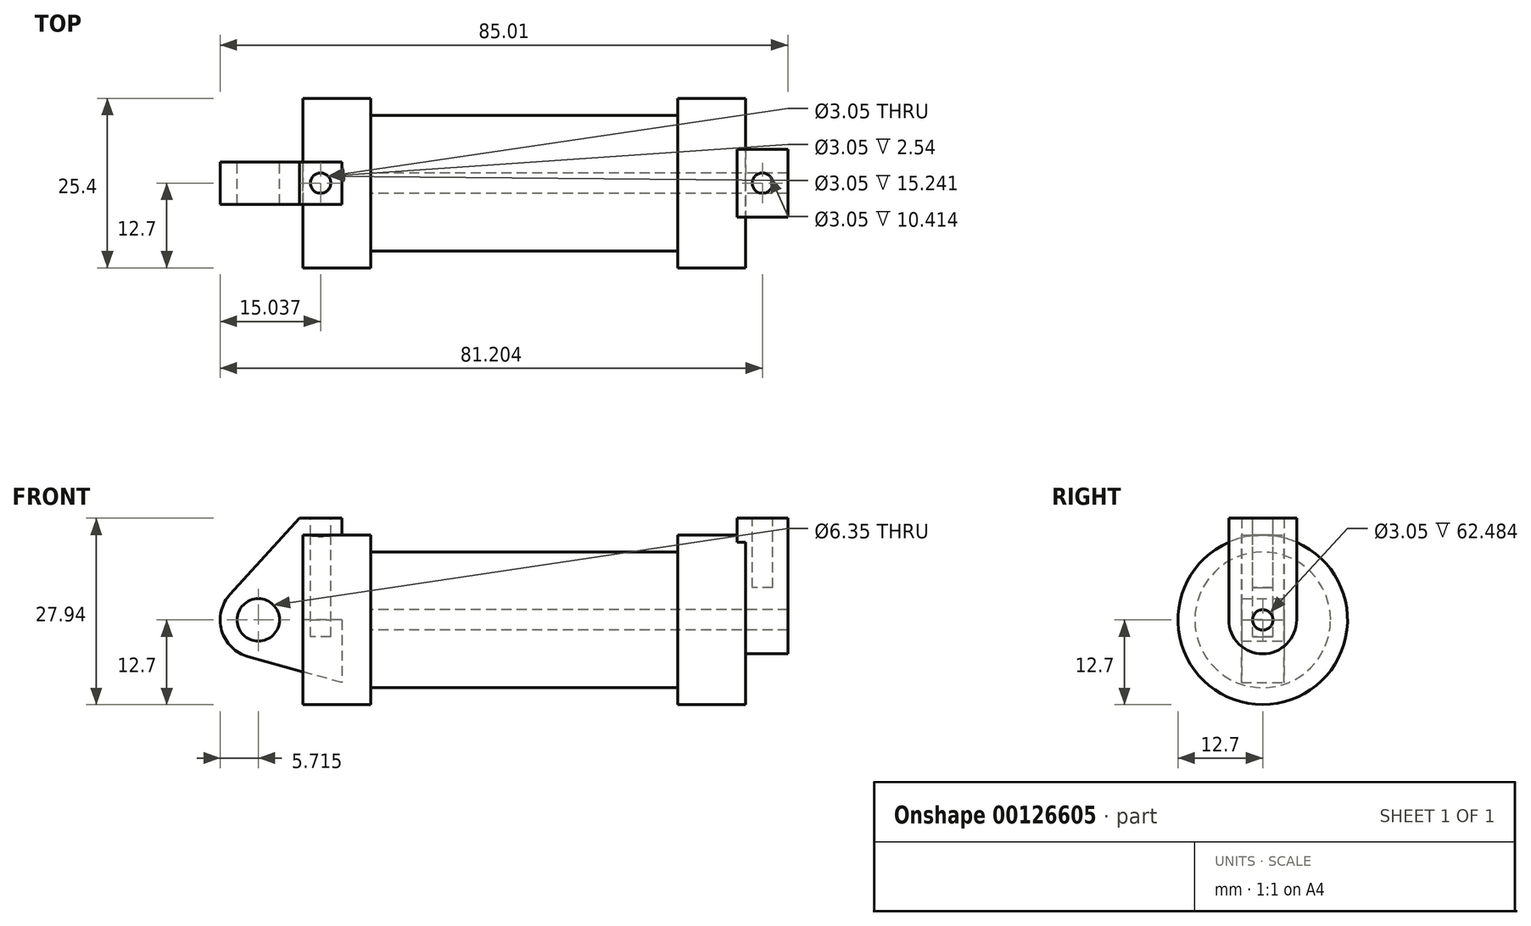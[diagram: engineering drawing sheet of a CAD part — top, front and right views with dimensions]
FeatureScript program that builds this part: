
annotation { "Feature Type Name" : "Feature", "Feature Type Description" : "" }
export const myFeature = defineFeature(function(context is Context, id is Id, definition is map)
    precondition{}
    {
        {
            var Q0;
            Q0=qCreatedBy(makeId("Front.planeOp"),FACE);
            var sketch = newSketch(context, id + "F0", { "sketchPlane" : qUnion([Q0])});
            skLineSegment(sketch, "E0", {"start": v(0, 0) * mm, "end": v(0, 12.7) * mm});
            skLineSegment(sketch, "E1", {"start": v(0, 12.7) * mm, "end": v(10.16, 12.7) * mm});
            skLineSegment(sketch, "E2", {"start": v(10.16, 12.7) * mm, "end": v(10.16, 10.16) * mm});
            skLineSegment(sketch, "E3", {"start": v(10.16, 10.16) * mm, "end": v(56.13, 10.16) * mm});
            skLineSegment(sketch, "E4", {"start": v(56.13, 10.16) * mm, "end": v(56.13, 12.7) * mm});
            skLineSegment(sketch, "E5", {"start": v(56.13, 12.7) * mm, "end": v(66.3, 12.7) * mm});
            skLineSegment(sketch, "E6", {"start": v(66.3, 12.7) * mm, "end": v(66.3, 0) * mm});
            skLineSegment(sketch, "E7", {"start": v(66.3, 0) * mm, "end": v(0, 0) * mm});
            skLineSegment(sketch, "E8", {"start": v(5.84, 15.24) * mm, "end": v(-0.5, 15.24) * mm});
            skLineSegment(sketch, "E9", {"start": v(-0.5, 15.24) * mm, "end": v(-10.88, 3.85) * mm});
            skLineSegment(sketch, "E10", {"start": v(0, 0) * mm, "end": v(-6.65, 0) * mm});
            skCircle(sketch, "E11", {"center": v(-6.65, 0) * mm, "radius": 5.72 * mm});
            skCircle(sketch, "E12", {"center": v(-6.65, 0) * mm, "radius": 3.18 * mm});
            skLineSegment(sketch, "E13", {"start": v(5.84, 15.24) * mm, "end": v(5.84, -9.4) * mm});
            skLineSegment(sketch, "E14", {"start": v(5.84, -9.4) * mm, "end": v(-8.18, -5.5) * mm});
            skSolve(sketch);
        }
        {
            var Q0;
            {var subQ0=sQuery(id+"F0.wireOp",EDGE,"E0");Q0=makeQuery(id+"F0.imprint","IMPRINT",FACE,{"disambiguationData":[TD([[makeQuery(id+"F0.imprint","IMPRINT",EDGE,{"derivedFrom":subQ0}),-1.0]])]});}
            var Q1;
            {var subQ0=sQuery(id+"F0.wireOp",EDGE,"E2");Q1=makeQuery(id+"F0.imprint","IMPRINT",FACE,{"disambiguationData":[TD([[makeQuery(id+"F0.imprint","IMPRINT",EDGE,{"derivedFrom":subQ0}),-1.0]])]});}
            var Q2;
            Q2=sQuery(id+"F0.wireOp",EDGE,"E10");
            revolve(context, id + "F1", {"entities" : qUnion([Q0, Q1]), "axis" : qUnion([Q2]), "revolveType" : RevolveType.FULL});
        }
        {
            var Q0;
            {var subQ3=sQuery(id+"F0.wireOp",EDGE,"E0");Q0=makeQuery(id+"F0.imprint","IMPRINT",FACE,{"disambiguationData":[TD([[makeQuery(id+"F0.imprint","IMPRINT",EDGE,{"derivedFrom":subQ3}),1.0]])]});}
            var Q1;
            {var subQ0=sQuery(id+"F0.wireOp",EDGE,"E14");Q1=makeQuery(id+"F0.imprint","IMPRINT",FACE,{"disambiguationData":[TD([[makeQuery(id+"F0.imprint","IMPRINT",EDGE,{"derivedFrom":subQ0}),-1.0]])]});}
            extrude(context, id + "F2", {"entities" : qUnion([Q0, Q1]), "depth" : 3.17 * mm, "hasSecondDirection" : true, "secondDirectionOppositeDirection" : true, "secondDirectionDepth" : 3.17 * mm});
        }
        {
            var Q0;
            {var subQ4=sQuery(id+"F0.wireOp",EDGE,"E12");Q0=makeQuery(id+"F0.imprint","IMPRINT",FACE,{"disambiguationData":[TD([[makeQuery(id+"F0.imprint","IMPRINT",EDGE,{"derivedFrom":subQ4}),-1.0]])]});}
            extrude(context, id + "F3", {"entities" : qUnion([Q0]), "operationType" : NewBodyOperationType.ADD, "depth" : 3.17 * mm, "hasSecondDirection" : true, "secondDirectionOppositeDirection" : true, "secondDirectionDepth" : 3.17 * mm});
        }
        {
            var Q0;
            Q0=makeQuery(id+"F1.opRevolve","SWEPT_FACE",FACE,{"disambiguationData":[OSD([sQuery(id+"F0.wireOp",EDGE,"E6")])]});
            var sketch = newSketch(context, id + "F4", { "sketchPlane" : qUnion([Q0])});
            skCircle(sketch, "E15", {"center": v(0, 0) * mm, "radius": 5.08 * mm});
            skLineSegment(sketch, "E16", {"start": v(5.08, 0) * mm, "end": v(5.08, 15.24) * mm});
            skLineSegment(sketch, "E17", {"start": v(5.08, 15.24) * mm, "end": v(-5.08, 15.24) * mm});
            skLineSegment(sketch, "E18", {"start": v(-5.08, 15.24) * mm, "end": v(-5.08, 0) * mm});
            skCircle(sketch, "E19", {"center": v(0, 0) * mm, "radius": 1.52 * mm});
            skSolve(sketch);
        }
        {
            var Q0;
            Q0 = qSketchRegion(id + "F4", true);
            extrude(context, id + "F5", {"entities" : qUnion([Q0]), "operationType" : NewBodyOperationType.ADD, "depth" : 6.35 * mm, "hasSecondDirection" : true, "secondDirectionOppositeDirection" : true, "secondDirectionDepth" : 1.27 * mm});
        }
        {
            var Q0;
            Q0=makeQuery(id+"F5.boolean.opBoolean","SPLIT",FACE,{"disambiguationData":[TD([makeQuery(id+"F5.opExtrude","SWEPT_FACE",FACE,{"disambiguationData":[OSD([sQuery(id+"F4.wireOp",EDGE,"E19")])]})])],"derivedFrom":makeQuery(id+"F1.opRevolve","SWEPT_FACE",FACE,{"disambiguationData":[OSD([sQuery(id+"F0.wireOp",EDGE,"E6")])]})});
            var Q1;
            Q1=makeQuery(id+"F1.opRevolve","SWEPT_FACE",FACE,{"disambiguationData":[OSD([sQuery(id+"F0.wireOp",EDGE,"E2")])]});
            extrude(context, id + "F6", {"entities" : qUnion([Q0]), "operationType" : NewBodyOperationType.REMOVE, "endBound" : BoundingType.UP_TO_SURFACE, "oppositeDirection" : true, "endBoundEntityFace" : qUnion([Q1]), "depth" : 25.4 * mm});
        }
        {
            var Q0;
            Q0=makeQuery(id+"F2.opExtrude","SWEPT_FACE",FACE,{"disambiguationData":[OSD([sQuery(id+"F0.wireOp",EDGE,"E8")])]});
            var sketch = newSketch(context, id + "F7", { "sketchPlane" : qUnion([Q0])});
            skCircle(sketch, "E20", {"center": v(2.67, 0) * mm, "radius": 1.52 * mm});
            skPoint(sketch, "E20.centerSnap0", {"position": v(-0.5, 0) * mm});
            skPoint(sketch, "E20.centerSnap1", {"position": v(2.67, 3.18) * mm});
            skSolve(sketch);
        }
        {
            var Q0;
            Q0 = qSketchRegion(id + "F7", true);
            extrude(context, id + "F8", {"entities" : qUnion([Q0]), "operationType" : NewBodyOperationType.REMOVE, "oppositeDirection" : true, "depth" : 17.78 * mm});
        }
        {
            var Q0;
            Q0=makeQuery(id+"F5.opExtrude","SWEPT_FACE",FACE,{"disambiguationData":[OSD([sQuery(id+"F4.wireOp",EDGE,"E17")])]});
            var sketch = newSketch(context, id + "F9", { "sketchPlane" : qUnion([Q0])});
            skCircle(sketch, "E21", {"center": v(68.83, 0) * mm, "radius": 1.52 * mm});
            skPoint(sketch, "E21.centerSnap0", {"position": v(65.02, 0) * mm});
            skPoint(sketch, "E21.centerSnap1", {"position": v(68.83, 5.08) * mm});
            skSolve(sketch);
        }
        {
            var Q0;
            Q0=makeQuery(id+"F9.imprint","IMPRINT",FACE,{"disambiguationData":[TD([[makeQuery(id+"F9.imprint","IMPRINT",EDGE,{"derivedFrom":sQuery(id+"F9.wireOp",EDGE,"E21")}),1.0]])]});
            extrude(context, id + "F10", {"entities" : qUnion([Q0]), "operationType" : NewBodyOperationType.REMOVE, "oppositeDirection" : true, "depth" : 10.4 * mm});
        }
    });
